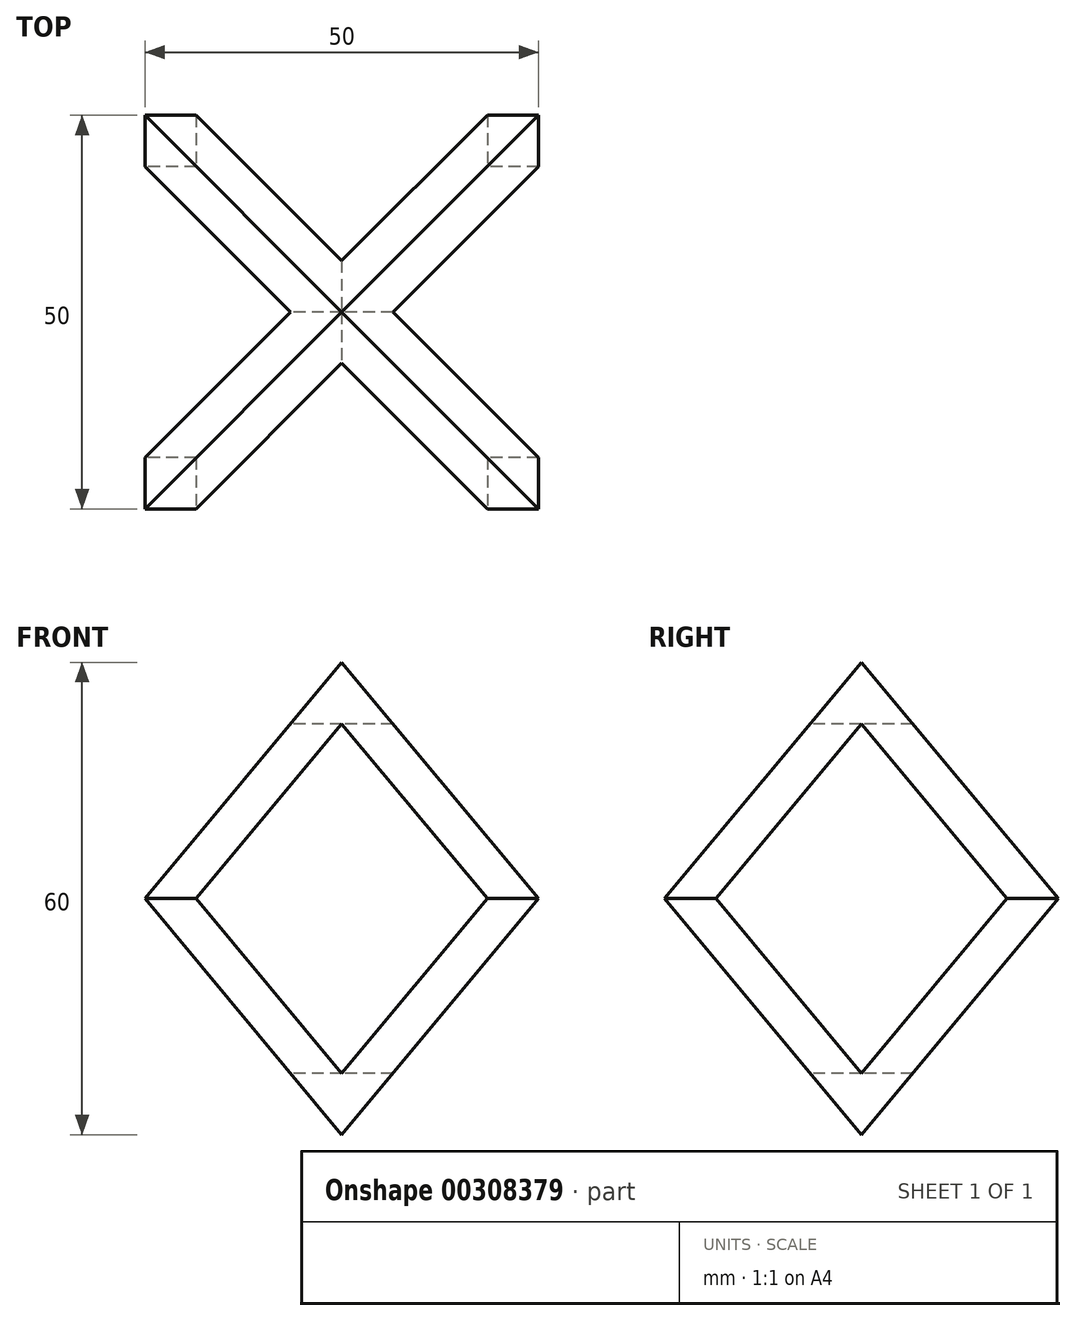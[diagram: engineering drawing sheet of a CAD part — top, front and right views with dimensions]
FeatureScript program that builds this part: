
annotation { "Feature Type Name" : "Feature", "Feature Type Description" : "" }
export const myFeature = defineFeature(function(context is Context, id is Id, definition is map)
    precondition{}
    {
        {
            var Q0;
            Q0=qCreatedBy(makeId("Top.planeOp"),FACE);
            var sketch = newSketch(context, id + "F0", { "sketchPlane" : qUnion([Q0])});
            skLineSegment(sketch, "E0.bottom", {"start": v(0, 0) * mm, "end": v(50, 0) * mm});
            skLineSegment(sketch, "E0.top", {"start": v(0, 50) * mm, "end": v(50, 50) * mm});
            skLineSegment(sketch, "E0.left", {"start": v(0, 0) * mm, "end": v(0, 50) * mm});
            skLineSegment(sketch, "E0.right", {"start": v(50, 0) * mm, "end": v(50, 50) * mm});
            skSolve(sketch);
        }
        {
            var Q0;
            Q0 = qSketchRegion(id + "F0", true);
            extrude(context, id + "F1", {"entities" : qUnion([Q0]), "depth" : 60 * mm});
        }
        {
            var Q0;
            Q0=makeQuery(id+"F1.opExtrude","SWEPT_FACE",FACE,{"disambiguationData":[OSD([sQuery(id+"F0.wireOp",EDGE,"E0.bottom")])]});
            var sketch = newSketch(context, id + "F2", { "sketchPlane" : qUnion([Q0])});
            skLineSegment(sketch, "E1", {"start": v(25, 60) * mm, "end": v(0, 30) * mm});
            skLineSegment(sketch, "E2", {"start": v(0, 30) * mm, "end": v(25, 0) * mm});
            skLineSegment(sketch, "E3", {"start": v(25, 0) * mm, "end": v(50, 30) * mm});
            skLineSegment(sketch, "E4", {"start": v(50, 30) * mm, "end": v(25, 60) * mm});
            skLineSegment(sketch, "E5", {"start": v(6.5, 30) * mm, "end": v(25, 52.19) * mm});
            skLineSegment(sketch, "E6", {"start": v(25, 52.19) * mm, "end": v(43.5, 30) * mm});
            skLineSegment(sketch, "E7", {"start": v(43.5, 30) * mm, "end": v(25, 7.81) * mm});
            skLineSegment(sketch, "E8", {"start": v(25, 7.81) * mm, "end": v(6.5, 30) * mm});
            skLineSegment(sketch, "E9", {"start": v(11.8, 44.17) * mm, "end": v(15.65, 40.96) * mm, "construction": true});
            skSolve(sketch);
        }
        {
            var Q0;
            Q0=makeQuery(id+"F1.opExtrude","SWEPT_FACE",FACE,{"disambiguationData":[OSD([sQuery(id+"F0.wireOp",EDGE,"E0.left")])]});
            var sketch = newSketch(context, id + "F3", { "sketchPlane" : qUnion([Q0])});
            skLineSegment(sketch, "E10", {"start": v(-25, 0) * mm, "end": v(-50, 30) * mm});
            skLineSegment(sketch, "E11", {"start": v(-50, 30) * mm, "end": v(-25, 60) * mm});
            skLineSegment(sketch, "E12", {"start": v(-25, 60) * mm, "end": v(0, 30) * mm});
            skLineSegment(sketch, "E13", {"start": v(0, 30) * mm, "end": v(-25, 0) * mm});
            skLineSegment(sketch, "E14", {"start": v(-25, 7.81) * mm, "end": v(-43.5, 30) * mm});
            skLineSegment(sketch, "E15", {"start": v(-43.5, 30) * mm, "end": v(-25, 52.19) * mm});
            skLineSegment(sketch, "E16", {"start": v(-25, 52.19) * mm, "end": v(-6.5, 30) * mm});
            skLineSegment(sketch, "E17", {"start": v(-6.5, 30) * mm, "end": v(-25, 7.81) * mm});
            skLineSegment(sketch, "E18", {"start": v(-40.06, 41.93) * mm, "end": v(-36.22, 38.73) * mm, "construction": true});
            skSolve(sketch);
        }
        {
            var Q0;
            Q0 = qSketchRegion(id + "F2", true);
            extrude(context, id + "F4", {"entities" : qUnion([Q0]), "operationType" : NewBodyOperationType.INTERSECT, "endBound" : BoundingType.THROUGH_ALL, "oppositeDirection" : true, "depth" : 25 * mm});
        }
        {
            var Q0;
            Q0 = qSketchRegion(id + "F3", true);
            extrude(context, id + "F5", {"entities" : qUnion([Q0]), "operationType" : NewBodyOperationType.INTERSECT, "endBound" : BoundingType.THROUGH_ALL, "oppositeDirection" : true, "depth" : 25 * mm});
        }
    });
